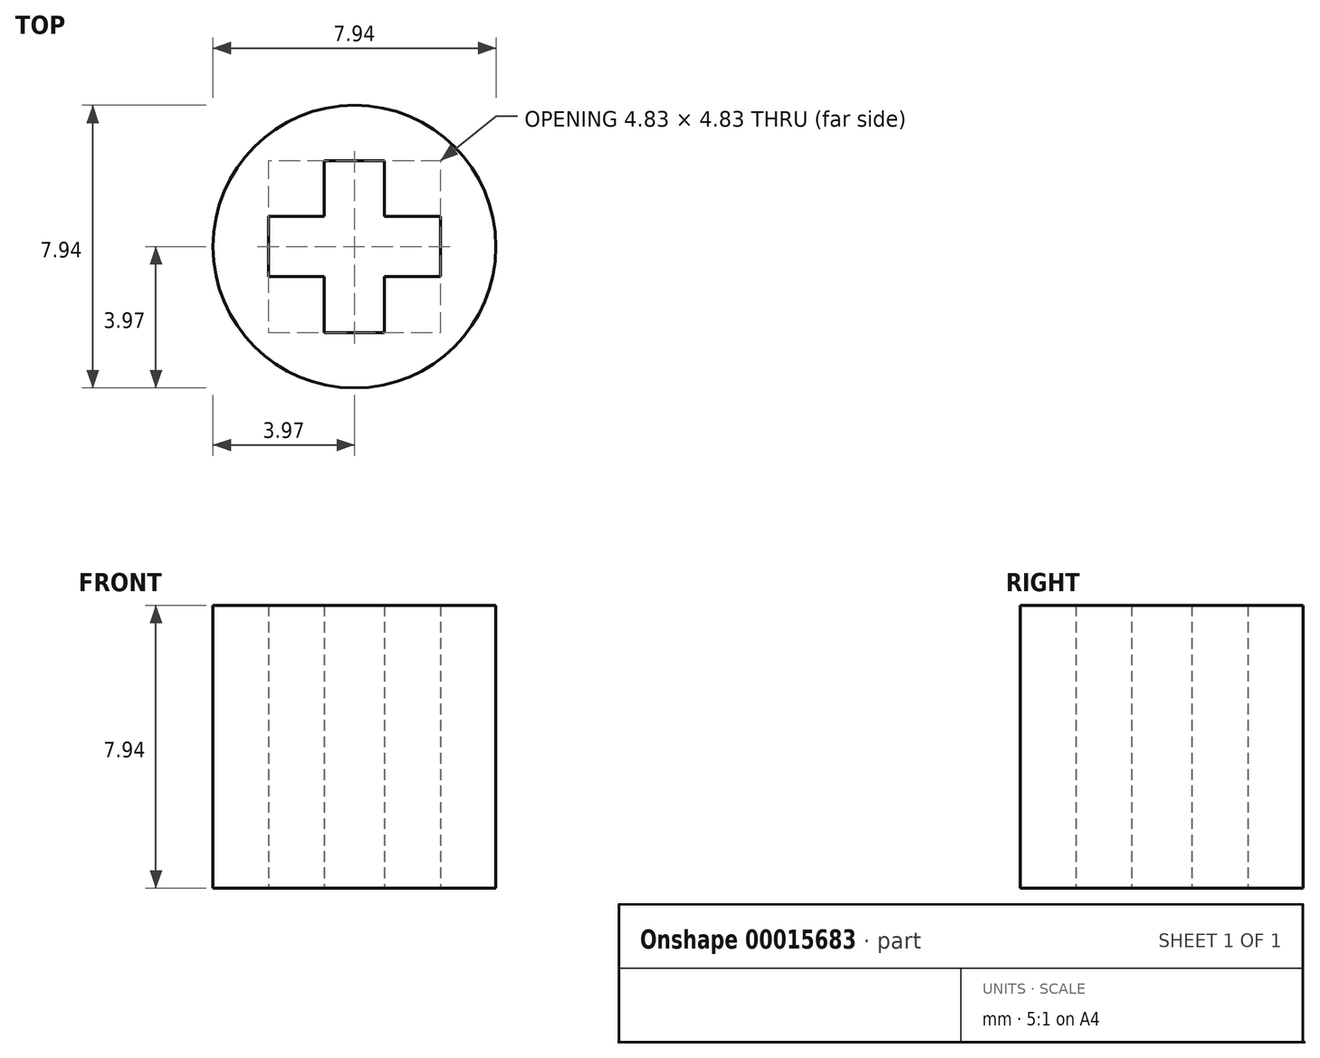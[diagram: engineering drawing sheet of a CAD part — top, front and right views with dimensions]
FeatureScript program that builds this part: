
annotation { "Feature Type Name" : "Feature", "Feature Type Description" : "" }
export const myFeature = defineFeature(function(context is Context, id is Id, definition is map)
    precondition{}
    {
        {
            var Q0;
            Q0=qCreatedBy(makeId("Top.planeOp"),FACE);
            var sketch = newSketch(context, id + "F0", { "sketchPlane" : qUnion([Q0])});
            skCircle(sketch, "E0", {"center": v(0, 0) * mm, "radius": 3.97 * mm});
            skLineSegment(sketch, "E1.rect.bottom", {"start": v(0.84, -2.41) * mm, "end": v(-0.84, -2.41) * mm});
            skLineSegment(sketch, "E1.rect.top", {"start": v(0.84, 2.41) * mm, "end": v(-0.84, 2.41) * mm});
            skLineSegment(sketch, "E1.rect.left", {"start": v(0.84, -2.41) * mm, "end": v(0.84, 2.41) * mm});
            skLineSegment(sketch, "E1.rect.right", {"start": v(-0.84, -2.41) * mm, "end": v(-0.84, 2.41) * mm});
            skLineSegment(sketch, "E2.rect.bottom", {"start": v(2.41, 0.84) * mm, "end": v(-2.41, 0.84) * mm});
            skLineSegment(sketch, "E2.rect.top", {"start": v(2.41, -0.84) * mm, "end": v(-2.41, -0.84) * mm});
            skLineSegment(sketch, "E2.rect.left", {"start": v(2.41, 0.84) * mm, "end": v(2.41, -0.84) * mm});
            skLineSegment(sketch, "E2.rect.right", {"start": v(-2.41, 0.84) * mm, "end": v(-2.41, -0.84) * mm});
            skSolve(sketch);
        }
        {
            var Q0;
            Q0=qSketchRegion(id+"F0",true);
            extrude(context, id + "F1", {"entities" : qUnion([Q0]), "depth" : 7.94 * mm});
        }
    });
